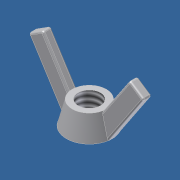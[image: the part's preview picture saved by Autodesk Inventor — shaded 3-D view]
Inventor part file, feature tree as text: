
AUTODESK INVENTOR PART (.ipt)
format: ipt  version: 2012 (Build 160160000, 160)  size: 126,976 bytes
history: native  units: in
note: dims shown in document units (in); Inventor stores cm internally (conversion verified against a paired STEP export)
features: extrude x2, sketch x1, revolve x1, fillet x1, hole x1
ambient origin geometry x8: Origin, YZ Plane, XZ Plane, XY Plane, X Axis, Y Axis, Z Axis, Center Point
bodies: Solid1 (feature_tree)
feature tree (6):
  sketch  "Sketch1"  dims[d0=0.125in d1=0.125in d3=0.15in d4=0.2in d5=0.2in d6=0.2in d8=0.55in d9=0.55in d10=90.0deg d11=0.075in d12=0.0in d13=0.075in d14=0.0in d15=0.015in d16=1.0in d17=1.0in d18=0.196in d19=0.5in d20=0.375in d21=0.25in d22=0.5635in d23=0.75in d24=0.8108in]
  revolve  "Revolution1"  [1 undecoded]
  extrude  "Extrusion1"  Depth=0.15in
  extrude  "Extrusion2"  Depth=0.2in
  fillet  "Fillet1"  Radius=0.2in
  hole  "Hole1"  [1 undecoded]
note: 2 required parameter values undecoded (feature->parameter linkage not recoverable at this tier; creation-order binding heuristic only, values carry confidence <= 0.55)